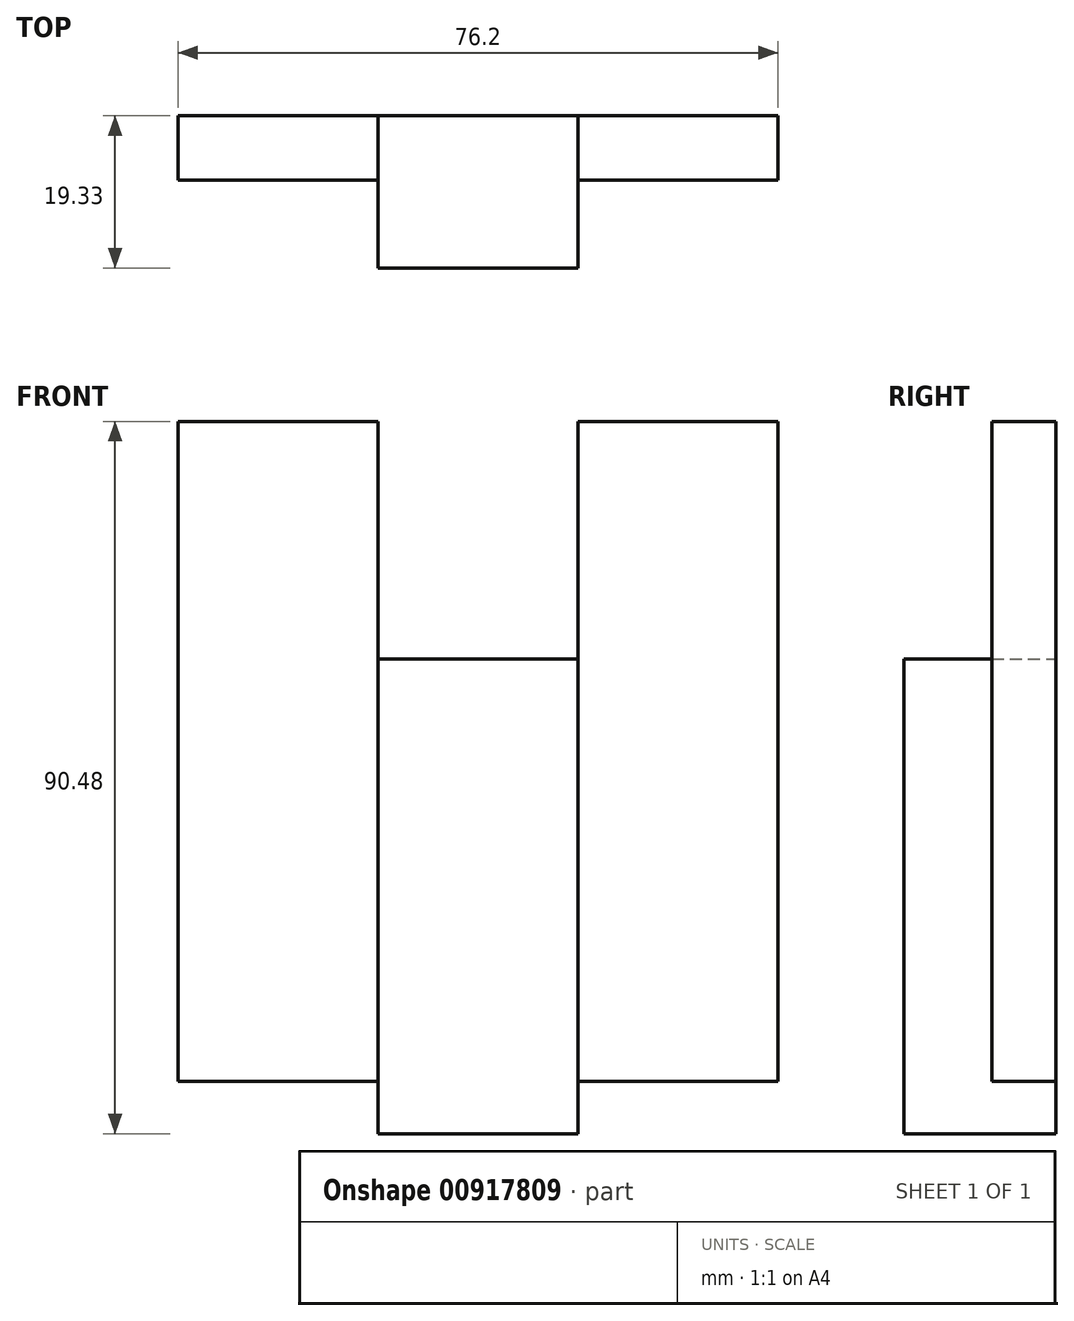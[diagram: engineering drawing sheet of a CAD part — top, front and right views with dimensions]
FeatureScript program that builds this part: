
annotation { "Feature Type Name" : "Feature", "Feature Type Description" : "" }
export const myFeature = defineFeature(function(context is Context, id is Id, definition is map)
    precondition{}
    {
        {
            var Q0;
            Q0=qCreatedBy(makeId("Front.planeOp"),FACE);
            var sketch = newSketch(context, id + "F0", { "sketchPlane" : qUnion([Q0])});
            skLineSegment(sketch, "E0", {"start": v(-50.8, 60.33) * mm, "end": v(-50.8, -23.5) * mm});
            skLineSegment(sketch, "E1", {"start": v(-50.8, -23.5) * mm, "end": v(25.4, -23.5) * mm});
            skLineSegment(sketch, "E2", {"start": v(25.4, -23.5) * mm, "end": v(25.4, 60.33) * mm});
            skLineSegment(sketch, "E3", {"start": v(-50.8, 60.32) * mm, "end": v(-25.4, 60.32) * mm});
            skLineSegment(sketch, "E4", {"start": v(25.4, 60.33) * mm, "end": v(0, 60.33) * mm});
            skLineSegment(sketch, "E5", {"start": v(-25.4, 60.32) * mm, "end": v(-25.4, 0) * mm});
            skLineSegment(sketch, "E6", {"start": v(0, 60.33) * mm, "end": v(0, 0) * mm});
            skLineSegment(sketch, "E7", {"start": v(0, 0) * mm, "end": v(-25.4, 0) * mm});
            skSolve(sketch);
        }
        {
            var Q0;
            Q0 = qSketchRegion(id + "F0", true);
            extrude(context, id + "F1", {"entities" : qUnion([Q0]), "depth" : 8.16 * mm, "offsetDistance" : 25.4 * mm});
        }
        {
            var Q0;
            Q0=qCreatedBy(makeId("Front.planeOp"),FACE);
            var sketch = newSketch(context, id + "F2", { "sketchPlane" : qUnion([Q0])});
            skLineSegment(sketch, "E8.bottom", {"start": v(0, -30.16) * mm, "end": v(-25.4, -30.16) * mm});
            skLineSegment(sketch, "E8.top", {"start": v(0, 30.16) * mm, "end": v(-25.4, 30.16) * mm});
            skLineSegment(sketch, "E8.left", {"start": v(0, -30.16) * mm, "end": v(0, 30.16) * mm});
            skLineSegment(sketch, "E8.right", {"start": v(-25.4, -30.16) * mm, "end": v(-25.4, 30.16) * mm});
            skPoint(sketch, "E8.middle", {"position": v(-12.7, 0) * mm});
            skSolve(sketch);
        }
        {
            var Q0;
            Q0=makeQuery(id+"F2.imprint","IMPRINT",FACE,{"disambiguationData":[TD([[makeQuery(id+"F2.imprint","IMPRINT",EDGE,{"derivedFrom":sQuery(id+"F2.wireOp",EDGE,"E8.bottom")}),-1.0]])]});
            extrude(context, id + "F3", {"entities" : qUnion([Q0]), "operationType" : NewBodyOperationType.ADD, "depth" : 19.33 * mm, "offsetDistance" : 25.4 * mm});
        }
    });
